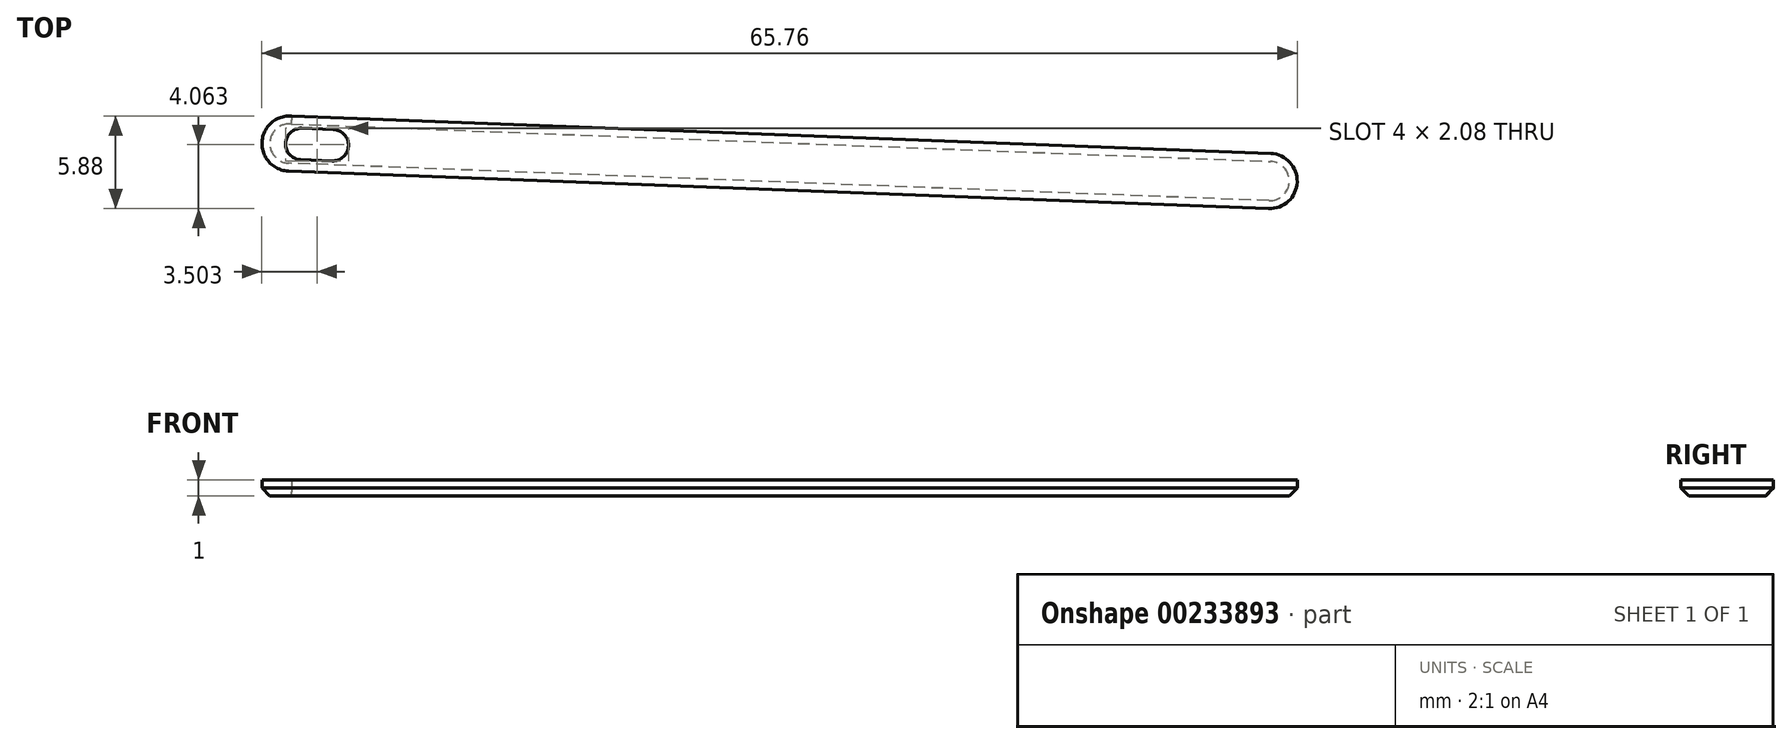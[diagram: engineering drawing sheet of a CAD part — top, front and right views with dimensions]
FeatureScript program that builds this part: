
annotation { "Feature Type Name" : "Feature", "Feature Type Description" : "" }
export const myFeature = defineFeature(function(context is Context, id is Id, definition is map)
    precondition{}
    {
        {
            var Q0;
            Q0=qCreatedBy(makeId("Top.planeOp"),FACE);
            var sketch = newSketch(context, id + "F0", { "sketchPlane" : qUnion([Q0])});
            skArc(sketch, "E0", {"start": v(-1.43, 1.74) * mm, "mid": v(-3.31, 0.1) * mm, "end": v(-1.63, -1.75) * mm});
            skArc(sketch, "E1", {"start": v(60.62, -4.13) * mm, "mid": v(62.44, -2.45) * mm, "end": v(60.76, -0.63) * mm});
            skLineSegment(sketch, "E2", {"start": v(-1.43, 1.74) * mm, "end": v(60.76, -0.63) * mm});
            skLineSegment(sketch, "E3", {"start": v(-1.63, -1.75) * mm, "end": v(60.62, -4.13) * mm});
            skLineSegment(sketch, "E4", {"start": v(-1.57, 0) * mm, "end": v(60.69, -2.38) * mm, "construction": true});
            skArc(sketch, "E5", {"start": v(-0.78, 0.97) * mm, "mid": v(-1.82, 0) * mm, "end": v(-0.85, -1.03) * mm});
            skArc(sketch, "E6", {"start": v(1.14, -1.1) * mm, "mid": v(2.18, -0.14) * mm, "end": v(1.22, 0.9) * mm});
            skLineSegment(sketch, "E7", {"start": v(-0.78, 0.97) * mm, "end": v(1.22, 0.9) * mm});
            skLineSegment(sketch, "E8", {"start": v(-0.85, -1.03) * mm, "end": v(1.14, -1.1) * mm});
            skSolve(sketch);
        }
        {
            var Q0;
            {var subQ8=sQuery(id+"F0.wireOp",EDGE,"E3");Q0=makeQuery(id+"F0.imprint","IMPRINT",FACE,{"disambiguationData":[TD([[makeQuery(id+"F0.imprint","IMPRINT",EDGE,{"derivedFrom":subQ8}),1.0]])]});}
            var Q1;
            {var subQ0=sQuery(id+"F0.wireOp",EDGE,"E0");var subQ1=makeQuery(id+"F0.imprint","INTERSECT",VERTEX,{"derivedFrom":[subQ0,sQuery(id+"F0.wireOp",EDGE,"E2")]});Q1=makeQuery(id+"F0.imprint","IMPRINT",FACE,{"disambiguationData":[TD([[makeQuery(id+"F0.imprint","IMPRINT",EDGE,{"disambiguationData":[TD([[subQ1,-1.0]])],"derivedFrom":subQ0}),1.0]])]});}
            var Q2;
            {var subQ0=sQuery(id+"F0.wireOp",EDGE,"E1");var subQ1=makeQuery(id+"F0.imprint","INTERSECT",VERTEX,{"derivedFrom":[subQ0,sQuery(id+"F0.wireOp",EDGE,"E2")]});Q2=makeQuery(id+"F0.imprint","IMPRINT",FACE,{"disambiguationData":[TD([[makeQuery(id+"F0.imprint","IMPRINT",EDGE,{"disambiguationData":[TD([[subQ1,-1.0]])],"derivedFrom":subQ0}),1.0]])]});}
            extrude(context, id + "F1", {"entities" : qUnion([Q0, Q1, Q2]), "depth" : 1 * mm});
        }
        {
            var Q0;
            Q0=makeQuery(id+"F1.opExtrude","CAP_EDGE",EDGE,{"disambiguationData":[OSD([sQuery(id+"F0.wireOp",EDGE,"E3")])],"isStart":true});
            chamfer(context, id + "F2", {"entities" : qUnion([Q0]), "width" : 0.5 * mm, "tangentPropagation" : true});
        }
    });
